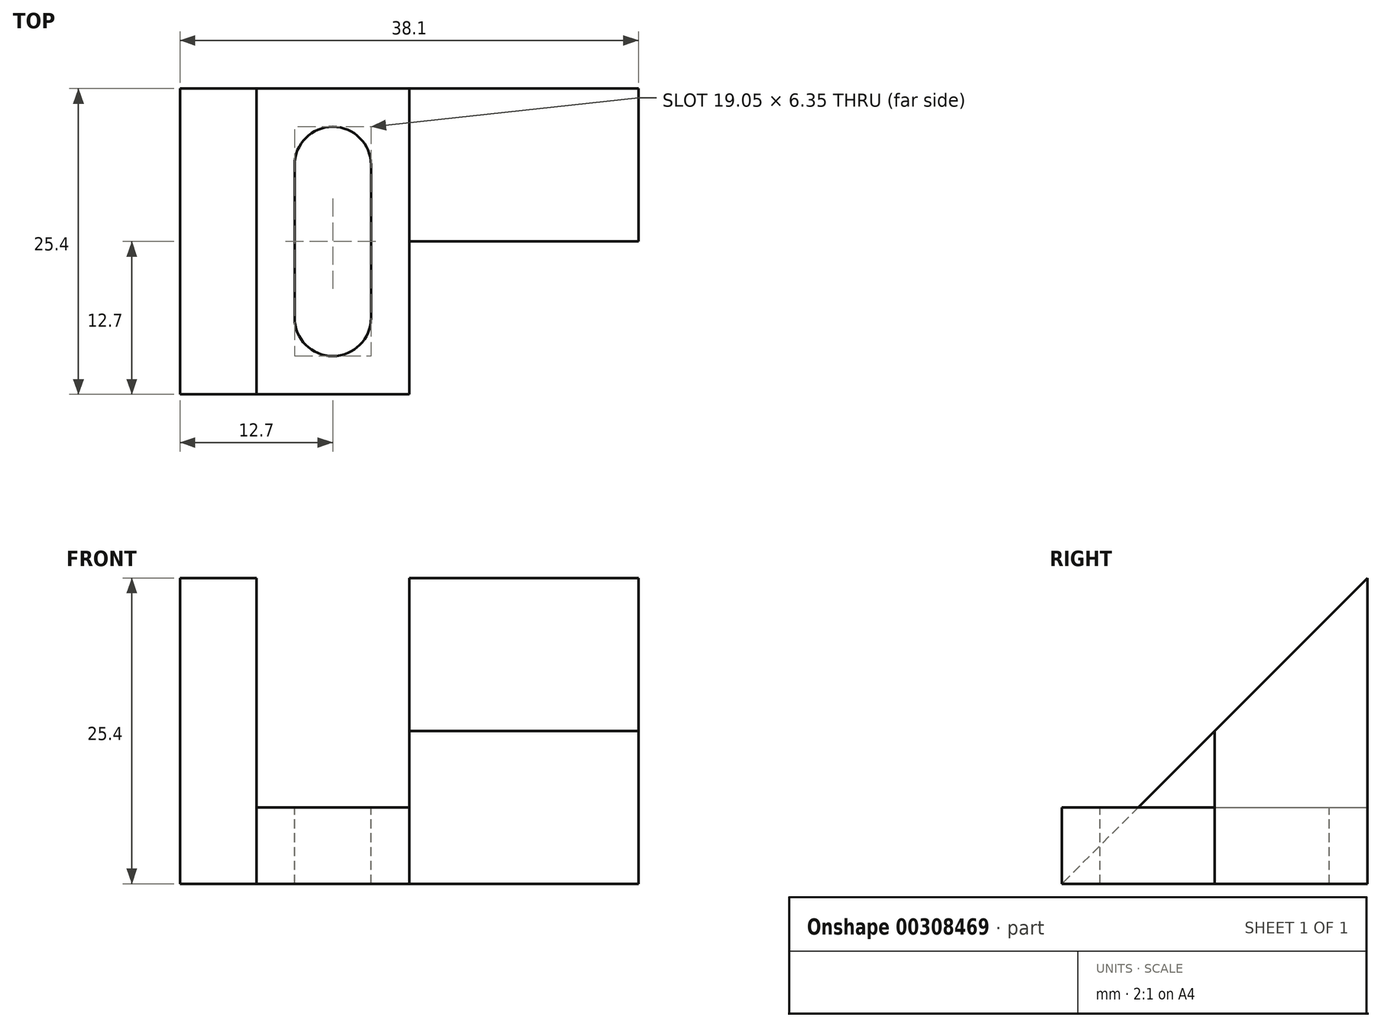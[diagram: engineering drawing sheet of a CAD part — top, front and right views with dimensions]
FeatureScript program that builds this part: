
annotation { "Feature Type Name" : "Feature", "Feature Type Description" : "" }
export const myFeature = defineFeature(function(context is Context, id is Id, definition is map)
    precondition{}
    {
        {
            var Q0;
            Q0=qCreatedBy(makeId("Right.planeOp"),FACE);
            var sketch = newSketch(context, id + "F0", { "sketchPlane" : qUnion([Q0])});
            skLineSegment(sketch, "E0", {"start": v(0, 0) * mm, "end": v(25.4, 0) * mm});
            skLineSegment(sketch, "E1", {"start": v(25.4, 0) * mm, "end": v(25.4, 25.4) * mm});
            skLineSegment(sketch, "E2", {"start": v(25.4, 25.4) * mm, "end": v(0, 0) * mm});
            skSolve(sketch);
        }
        {
            var Q0;
            Q0 = qSketchRegion(id + "F0", true);
            extrude(context, id + "F1", {"entities" : qUnion([Q0]), "depth" : 6.35 * mm});
        }
        {
            var Q0;
            Q0=makeQuery(id+"F1.opExtrude","CAP_FACE",FACE,{"disambiguationData":[OSD([sQuery(id+"F0.wireOp",EDGE,"E0"),sQuery(id+"F0.wireOp",EDGE,"E1"),sQuery(id+"F0.wireOp",EDGE,"E2")])],"isStart":false});
            var sketch = newSketch(context, id + "F2", { "sketchPlane" : qUnion([Q0])});
            skLineSegment(sketch, "E3", {"start": v(0, 0) * mm, "end": v(0, 6.35) * mm});
            skLineSegment(sketch, "E4", {"start": v(0, 6.35) * mm, "end": v(25.4, 6.35) * mm});
            skLineSegment(sketch, "E5", {"start": v(25.4, 6.35) * mm, "end": v(25.4, 0) * mm});
            skLineSegment(sketch, "E6", {"start": v(25.4, 0) * mm, "end": v(0, 0) * mm});
            skSolve(sketch);
        }
        {
            var Q0;
            Q0 = qSketchRegion(id + "F2", true);
            extrude(context, id + "F3", {"entities" : qUnion([Q0]), "operationType" : NewBodyOperationType.ADD, "depth" : 12.7 * mm});
        }
        {
            var Q0;
            Q0=makeQuery(id+"F3.opExtrude","CAP_FACE",FACE,{"disambiguationData":[OSD([sQuery(id+"F2.wireOp",EDGE,"E3"),sQuery(id+"F2.wireOp",EDGE,"E4"),sQuery(id+"F2.wireOp",EDGE,"E5"),sQuery(id+"F2.wireOp",EDGE,"E6")])],"isStart":false});
            var sketch = newSketch(context, id + "F4", { "sketchPlane" : qUnion([Q0])});
            skLineSegment(sketch, "E7", {"start": v(12.7, 0) * mm, "end": v(25.4, 0) * mm});
            skLineSegment(sketch, "E8", {"start": v(25.4, 0) * mm, "end": v(25.4, 25.4) * mm});
            skLineSegment(sketch, "E9", {"start": v(25.4, 25.4) * mm, "end": v(12.7, 12.7) * mm});
            skLineSegment(sketch, "E10", {"start": v(12.7, 12.7) * mm, "end": v(12.7, 0) * mm});
            skSolve(sketch);
        }
        {
            var Q0;
            Q0 = qSketchRegion(id + "F4", true);
            extrude(context, id + "F5", {"entities" : qUnion([Q0]), "operationType" : NewBodyOperationType.ADD, "depth" : 19.05 * mm});
        }
        {
            var Q0;
            Q0=makeQuery(id+"F3.opExtrude","SWEPT_FACE",FACE,{"disambiguationData":[OSD([sQuery(id+"F2.wireOp",EDGE,"E4")])]});
            var sketch = newSketch(context, id + "F6", { "sketchPlane" : qUnion([Q0])});
            skLineSegment(sketch, "E11", {"start": v(15.88, 6.35) * mm, "end": v(15.87, 19.05) * mm});
            skLineSegment(sketch, "E12", {"start": v(15.87, 19.05) * mm, "end": v(9.53, 19.05) * mm, "construction": true});
            skLineSegment(sketch, "E13", {"start": v(9.52, 19.05) * mm, "end": v(9.52, 6.35) * mm});
            skLineSegment(sketch, "E14", {"start": v(9.53, 6.35) * mm, "end": v(15.88, 6.35) * mm, "construction": true});
            skLineSegment(sketch, "E15", {"start": v(12.7, 19.05) * mm, "end": v(12.7, 6.35) * mm, "construction": true});
            skArc(sketch, "E16", {"start": v(15.88, 19.05) * mm, "mid": v(12.7, 22.23) * mm, "end": v(9.52, 19.05) * mm});
            skArc(sketch, "E17", {"start": v(9.52, 6.35) * mm, "mid": v(12.7, 3.18) * mm, "end": v(15.88, 6.35) * mm});
            skSolve(sketch);
        }
        {
            var Q0;
            Q0 = qSketchRegion(id + "F6", true);
            extrude(context, id + "F7", {"entities" : qUnion([Q0]), "operationType" : NewBodyOperationType.REMOVE, "endBound" : BoundingType.THROUGH_ALL, "oppositeDirection" : true, "depth" : 25.4 * mm});
        }
    });
